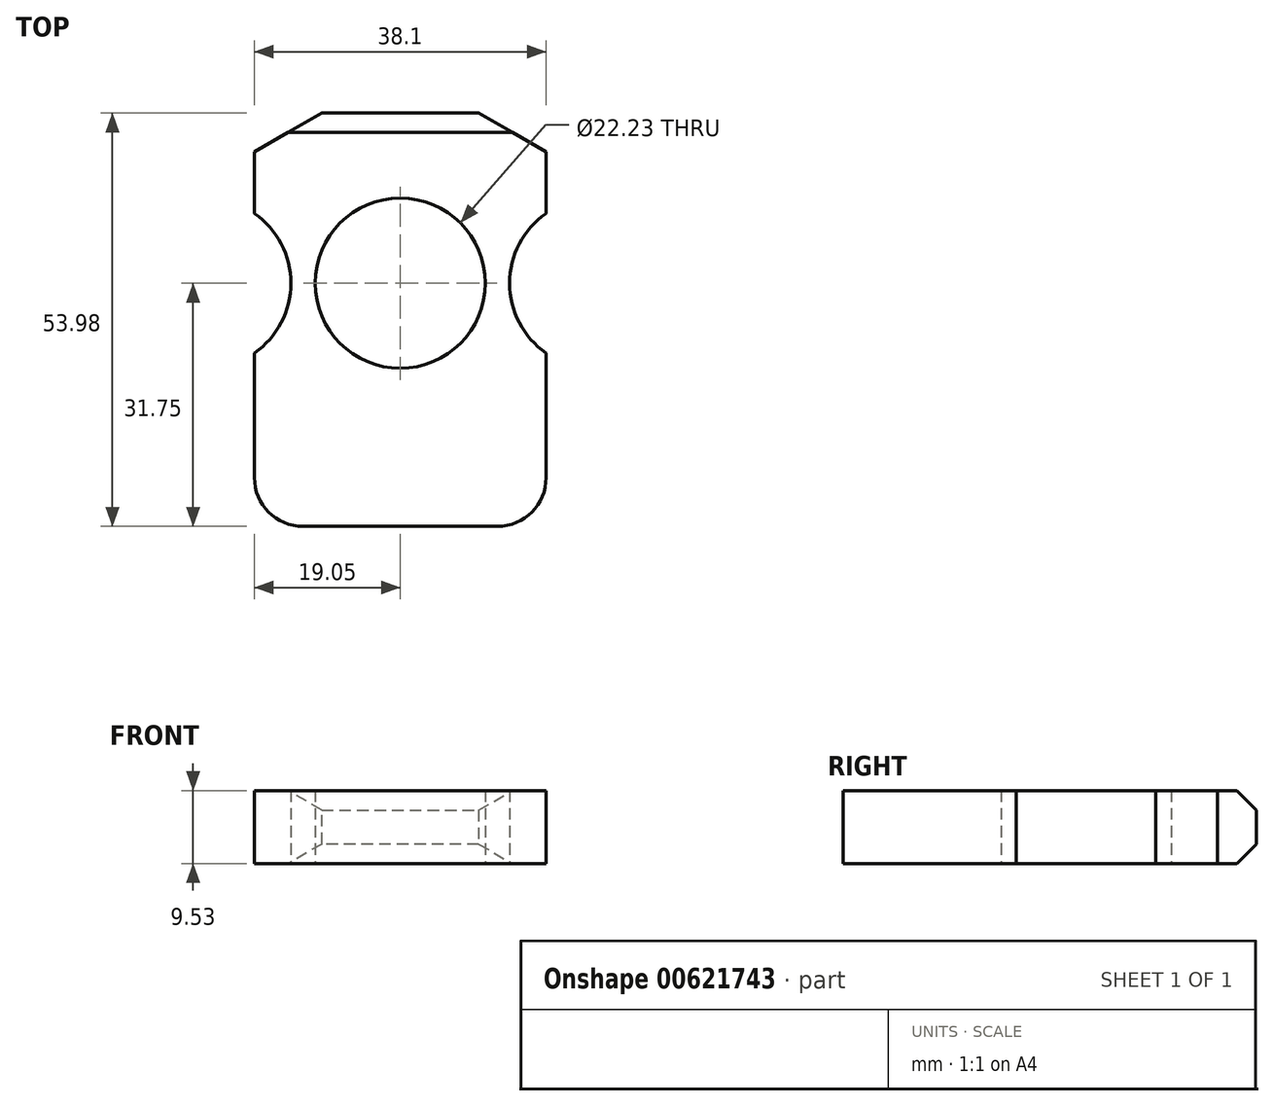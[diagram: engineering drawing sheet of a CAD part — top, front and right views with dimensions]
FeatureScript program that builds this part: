
annotation { "Feature Type Name" : "Feature", "Feature Type Description" : "" }
export const myFeature = defineFeature(function(context is Context, id is Id, definition is map)
    precondition{}
    {
        {
            var Q0;
            Q0=qCreatedBy(makeId("Top.planeOp"),FACE);
            var sketch = newSketch(context, id + "F0", { "sketchPlane" : qUnion([Q0])});
            skCircle(sketch, "E0", {"center": v(0, 0) * mm, "radius": 11.11 * mm});
            skLineSegment(sketch, "E1.bottom", {"start": v(-19.05, 22.22) * mm, "end": v(19.05, 22.23) * mm});
            skLineSegment(sketch, "E1.top", {"start": v(-19.05, -31.75) * mm, "end": v(19.05, -31.75) * mm});
            skLineSegment(sketch, "E1.left", {"start": v(-19.05, 22.22) * mm, "end": v(-19.05, 9.12) * mm});
            skLineSegment(sketch, "E1.right", {"start": v(19.05, 22.23) * mm, "end": v(19.05, 9.12) * mm});
            skArc(sketch, "E2", {"start": v(-19.05, -9.12) * mm, "mid": v(-14.29, 0) * mm, "end": v(-19.05, 9.12) * mm});
            skArc(sketch, "E3", {"start": v(19.05, 9.12) * mm, "mid": v(14.29, 0) * mm, "end": v(19.05, -9.12) * mm});
            skLineSegment(sketch, "E4.trimOffspring", {"start": v(-19.05, -9.12) * mm, "end": v(-19.05, -31.75) * mm});
            skLineSegment(sketch, "E5.trimOffspring", {"start": v(19.05, -9.12) * mm, "end": v(19.05, -31.75) * mm});
            skSolve(sketch);
        }
        {
            var Q0;
            Q0 = qSketchRegion(id + "F0", true);
            extrude(context, id + "F1", {"entities" : qUnion([Q0]), "depth" : 9.52 * mm, "offsetDistance" : 25.4 * mm});
        }
        {
            var Q0;
            Q0=makeQuery(id+"F1.opExtrude","SWEPT_EDGE",EDGE,{"disambiguationData":[OSD([sQuery(id+"F0.wireOp",EDGE,"E1.bottom"),sQuery(id+"F0.wireOp",EDGE,"E1.left")])]});
            var Q1;
            Q1=makeQuery(id+"F1.opExtrude","SWEPT_EDGE",EDGE,{"disambiguationData":[OSD([sQuery(id+"F0.wireOp",EDGE,"E1.bottom"),sQuery(id+"F0.wireOp",EDGE,"E1.right")])]});
            chamfer(context, id + "F2", {"entities" : qUnion([Q0, Q1]), "chamferType" : ChamferType.OFFSET_ANGLE, "width" : 5.08 * mm, "oppositeDirection" : false, "angle" : 60 * degree, "tangentPropagation" : true});
        }
        {
            var Q0;
            Q0=makeQuery(id+"F1.opExtrude","CAP_EDGE",EDGE,{"disambiguationData":[OSD([sQuery(id+"F0.wireOp",EDGE,"E1.bottom")])],"isStart":false});
            var Q1;
            Q1=makeQuery(id+"F1.opExtrude","CAP_EDGE",EDGE,{"disambiguationData":[OSD([sQuery(id+"F0.wireOp",EDGE,"E1.bottom")])],"isStart":true});
            chamfer(context, id + "F3", {"entities" : qUnion([Q0, Q1]), "chamferType" : ChamferType.OFFSET_ANGLE, "width" : 2.54 * mm, "oppositeDirection" : false, "angle" : 45 * degree, "tangentPropagation" : true});
        }
        {
            var Q0;
            Q0=makeQuery(id+"F1.opExtrude","SWEPT_EDGE",EDGE,{"disambiguationData":[OSD([sQuery(id+"F0.wireOp",EDGE,"E1.top"),sQuery(id+"F0.wireOp",EDGE,"E5.trimOffspring")])]});
            var Q1;
            Q1=makeQuery(id+"F1.opExtrude","SWEPT_EDGE",EDGE,{"disambiguationData":[OSD([sQuery(id+"F0.wireOp",EDGE,"E1.top"),sQuery(id+"F0.wireOp",EDGE,"E4.trimOffspring")])]});
            fillet(context, id + "F4", {"entities" : qUnion([Q0, Q1]), "radius" : 6.35 * mm, "tangentPropagation" : true, "allowEdgeOverflow" : false});
        }
    });
